FCSTD DOCUMENT  (FreeCAD 1.0R39109 (Git))
Label: assembly_01
License: All rights reserved
LicenseURL: https://en.wikipedia.org/wiki/All_rights_reserved
objects: App::FeaturePython×7, App::Link×3, Assembly::JointGroup×1, Assembly::AssemblyObject×1
EXTERNAL_REF file=case_bottom_01.FCStd obj=Body
EXTERNAL_REF file=case_top_01.FCStd obj=Body
EXTERNAL_REF file=device.FCStd obj=Body

FEATURE [App::Link] Body
  LinkedObject = -> <external case_bottom_01.FCStd>#Body
FEATURE [App::FeaturePython] GroundedJoint  # Assembly grounded joint (typed FeaturePython)
  ObjectToGround = -> Body
FEATURE [App::Link] Body001
  LinkPlacement = pos=(-0.499998,0.5,82.9001) rot=(0,0,1;0rad)
  LinkedObject = -> <external case_top_01.FCStd>#Body
  Placement = pos=(-0.499998,0.5,82.9001) rot=(0,0,1;0rad)
FEATURE [App::Link] Body002
  LinkPlacement = pos=(30.0639,41.1692,54.1501) rot=(0,0,0.985027;0.00293rad)
  LinkedObject = -> <external device.FCStd>#Body
  Placement = pos=(30.0639,41.1692,54.1501) rot=(0,0,0.985027;0.00293rad)
FEATURE [App::FeaturePython] Joint  label="Cylindrical"  # Assembly joint (typed FeaturePython)
  Activated = true
  AngleMax = 0
  AngleMin = 0
  Detach1 = false
  Detach2 = false
  Distance = 0
  Distance2 = 0
  EnableAngleMax = false
  EnableAngleMin = false
  EnableLengthMax = false
  EnableLengthMin = false
  JointType = 2 (Cylindrical)
  LengthMax = 0
  LengthMin = 0
  Placement1 = pos=(-24,-21.1,-12.65) rot=(1,0,0;3.14159rad)
  Placement2 = pos=(6.125,20,6.2) rot=(0,0,1;0rad)
  Reference1 = -> Assembly [Body002.Edge17,Body002.Edge17]
  Reference2 = -> Assembly [Body.?Face125,Body.?Face125]
FEATURE [App::FeaturePython] Joint001  label="Cylindrical001"  # Assembly joint (typed FeaturePython)
  Activated = true
  AngleMax = 0
  AngleMin = 0
  Detach1 = false
  Detach2 = false
  Distance = 0
  Distance2 = 0
  EnableAngleMax = false
  EnableAngleMin = false
  EnableLengthMax = false
  EnableLengthMin = false
  JointType = 2 (Cylindrical)
  LengthMax = 0
  LengthMin = 0
  Placement1 = pos=(-8.85,30.67,-11.775) rot=(1,0,0;3.14159rad)
  Placement2 = pos=(21.125,72,6.2) rot=(0,0,1;0rad)
  Reference1 = -> Assembly [Body002.Face63,Body002.Face63]
  Reference2 = -> Assembly [Body.?Face130,Body.?Face130]
FEATURE [App::FeaturePython] Joint002  label="Distance"  # Assembly joint (typed FeaturePython)
  Activated = true
  AngleMax = 0
  AngleMin = 0
  Detach1 = false
  Detach2 = false
  Distance = 2
  Distance2 = 0
  EnableAngleMax = false
  EnableAngleMin = false
  EnableLengthMax = false
  EnableLengthMin = false
  JointType = 5 (Distance)
  LengthMax = 0
  LengthMin = 0
  Placement1 = pos=(21.125,72,4.5) rot=(0,0,1;0rad)
  Placement2 = pos=(-0.0391973,-1.25732,-12.65) rot=(0,0,1;0rad)
  Reference1 = -> Assembly [Body.Face138,Body.Vertex194]
  Reference2 = -> Assembly [Body002.Face3,Body002.Edge42]
FEATURE [App::FeaturePython] Joint003  label="Distance001"  # Assembly joint (typed FeaturePython)
  Activated = true
  AngleMax = 0
  AngleMin = 0
  Detach1 = false
  Detach2 = false
  Distance = 0
  Distance2 = 0
  EnableAngleMax = false
  EnableAngleMin = false
  EnableLengthMax = false
  EnableLengthMin = false
  JointType = 5 (Distance)
  LengthMax = 0
  LengthMin = 0
  Placement1 = pos=(30,78,-0.75) rot=(1,0,0;1.5708rad)
  Placement2 = pos=(30,78.5,20.95) rot=(0,0.707107,0.707107;3.14159rad)
  Reference1 = -> Assembly [Body001.Face23,Body001.Vertex22]
  Reference2 = -> Assembly [Body.Face101,Body.Face101]
FEATURE [App::FeaturePython] Joint004  label="Distance002"  # Assembly joint (typed FeaturePython)
  Activated = true
  AngleMax = 0
  AngleMin = 0
  Detach1 = false
  Detach2 = false
  Distance = 0
  Distance2 = 0
  EnableAngleMax = false
  EnableAngleMin = false
  EnableLengthMax = false
  EnableLengthMin = false
  JointType = 5 (Distance)
  LengthMax = 0
  LengthMin = 0
  Placement1 = pos=(2,40,-0.75) rot=(0.57735,0.57735,0.57735;2.0944rad)
  Placement2 = pos=(1.5,40,20.95) rot=(-0.57735,0.57735,0.57735;4.18879rad)
  Reference1 = -> Assembly [Body001.Face21,Body001.Face21]
  Reference2 = -> Assembly [Body.Face98,Body.Face98]
FEATURE [App::FeaturePython] Joint005  label="Distance003"  # Assembly joint (typed FeaturePython)
  Activated = true
  AngleMax = 0
  AngleMin = 0
  Detach1 = false
  Detach2 = false
  Distance = 0
  Distance2 = 0
  EnableAngleMax = false
  EnableAngleMin = false
  EnableLengthMax = false
  EnableLengthMin = false
  JointType = 5 (Distance)
  LengthMax = 0
  LengthMin = 0
  Placement1 = pos=(30,40,-2) rot=(0,0,1;0rad)
  Placement2 = pos=(30,40,19.9) rot=(0,0,1;0rad)
  Reference1 = -> Assembly [Body001.Face5,Body001.Vertex18]
  Reference2 = -> Assembly [Body.Face64,Body.Vertex106]
FEATURE [Assembly::JointGroup] Joints
  Group = -> [GroundedJoint,Joint,Joint001,Joint002,Joint003,Joint004,Joint005]
FEATURE [Assembly::AssemblyObject] Assembly
  Group = -> [Joints,Body,GroundedJoint,Body001,Body002,Joint,Joint001,Joint002,Joint003,Joint004,Joint005]
  Origin = -> Origin
  Type = Assembly

RESOLVED EXTERNAL PARTS (link-assembly join: the EXTERNAL_REF files above that resolve inside this repo's crawl, each included once):
---- part case_bottom_01.FCStd = doc fcstd_fc7d65538bb1 ----
FCSTD DOCUMENT  (FreeCAD 1.0R39109 (Git))
Label: case_bottom_01
License: All rights reserved
LicenseURL: https://en.wikipedia.org/wiki/All_rights_reserved
objects: Sketcher::SketchObject×11, PartDesign::Fillet×8, PartDesign::Pad×5, PartDesign::Pocket×4, PartDesign::PolarPattern×1, PartDesign::LinearPattern×1, PartDesign::Body×1
note: 78 computed .brp shape members not serialized (recipe doc carries the construction recipe); baked Part::Feature solids carry a one-line shape summary decoded from their .brp

FEATURE [Sketcher::SketchObject] Sketch
  ArcFitTolerance = 1e-06
  AttachmentSupport = -> [XY_Plane]
  FullyConstrained = true
  MakeInternals = false
  MapMode = 5
  sketch-geometry (4):
    g0: LineSegment StartX=0 StartY=0 StartZ=0 EndX=60 EndY=0 EndZ=0
    g1: LineSegment StartX=60 StartY=0 StartZ=0 EndX=60 EndY=80 EndZ=0
    g2: LineSegment StartX=60 StartY=80 StartZ=0 EndX=0 EndY=80 EndZ=0
    g3: LineSegment StartX=0 StartY=80 StartZ=0 EndX=0 EndY=0 EndZ=0
  constraints (11):
    c: Coincident(g0,g1)
    c: Coincident(g1,g2)
    c: Coincident(g2,g3)
    c: Coincident(g3,g0)
    c: Horizontal(g0)
    c: Horizontal(g2)
    c: Vertical(g1)
    c: Vertical(g3)
    c: Coincident(g0,g-1)
    c: DistanceY(g1,g1) = 80
    c: DistanceX(g2,g2) = 60
FEATURE [PartDesign::Pad] Pad
  Direction = (0,0,1)
  Length = 2.5
  Length2 = 10
  Profile = -> Sketch
  ReferenceAxis = -> Sketch [N_Axis]
  Refine = true
  Suppressed = false
  Type = 0
FEATURE [Sketcher::SketchObject] Sketch001
  ArcFitTolerance = 1e-06
  AttachmentSupport = -> [Pad]
  ExternalGeometry = -> [Pad]
  FullyConstrained = true
  MakeInternals = false
  MapMode = 5
  Placement = pos=(0,0,2.5) rot=(0,0,1;0rad)
  sketch-geometry (8):
    g0: LineSegment StartX=0 StartY=80 StartZ=0 EndX=0 EndY=0 EndZ=0
    g1: LineSegment StartX=0 StartY=0 StartZ=0 EndX=60 EndY=0 EndZ=0
    g2: LineSegment StartX=60 StartY=0 StartZ=0 EndX=60 EndY=80 EndZ=0
    g3: LineSegment StartX=60 StartY=80 StartZ=0 EndX=0 EndY=80 EndZ=0
    g4: LineSegment StartX=2.5 StartY=77.5 StartZ=0 EndX=2.5 EndY=2.5 EndZ=0
    g5: LineSegment StartX=2.5 StartY=2.5 StartZ=0 EndX=57.5 EndY=2.5 EndZ=0
    g6: LineSegment StartX=57.5 StartY=2.5 StartZ=0 EndX=57.5 EndY=77.5 EndZ=0
    g7: LineSegment StartX=57.5 StartY=77.5 StartZ=0 EndX=2.5 EndY=77.5 EndZ=0
  constraints (22):
    c: Coincident(g0,g1)
    c: Coincident(g1,g2)
    c: Coincident(g2,g3)
    c: Coincident(g3,g0)
    c: Vertical(g0)
    c: Vertical(g2)
    c: Horizontal(g1)
    c: Horizontal(g3)
    c: Coincident(g0,g-5)
    c: Coincident(g1,g-6)
    c: Coincident(g4,g5)
    c: Coincident(g5,g6)
    c: Coincident(g6,g7)
    c: Coincident(g7,g4)
    c: Vertical(g4)
    c: Vertical(g6)
    c: Horizontal(g5)
    c: Horizontal(g7)
    c: Distance(g3,g7) = 2.5
    c: Distance(g0,g4) = 2.5
    c: Distance(g2,g6) = 2.5
    c: Distance(g1,g5) = 2.5
FEATURE [PartDesign::Pad] Pad001
  BaseFeature = -> Pad
  Direction = (0,0,1)
  Length = 19.5
  Length2 = 10
  Profile = -> Sketch001
  ReferenceAxis = -> Sketch001 [N_Axis]
  Refine = true
  Suppressed = false
  Type = 0
FEATURE [Sketcher::SketchObject] Sketch002
  ArcFitTolerance = 1e-06
  AttachmentSupport = -> [Pad001]
  FullyConstrained = true
  MakeInternals = false
  MapMode = 5
  Placement = pos=(0,0,2.5) rot=(0,0,1;0rad)
FEATURE [Sketcher::SketchObject] Sketch003
  ArcFitTolerance = 1e-06
  AttachmentSupport = -> [Pad001]
  ExternalGeometry = -> [Pad001]
  FullyConstrained = true
  MakeInternals = false
  MapMode = 5
  Placement = pos=(0,0,2.5) rot=(0,0,1;0rad)
  sketch-geometry (6):
    g0: Circle CenterX=21.125 CenterY=72 CenterZ=0 NormalX=0 NormalY=0 NormalZ=1 AngleXU=0 Radius=5
    g1: Circle CenterX=48.625 CenterY=72 CenterZ=0 NormalX=0 NormalY=0 NormalZ=1 AngleXU=0 Radius=5
    g2: Circle CenterX=6.125 CenterY=20 CenterZ=0 NormalX=0 NormalY=0 NormalZ=1 AngleXU=0 Radius=5
    g3: Circle CenterX=53.875 CenterY=21 CenterZ=0 NormalX=0 NormalY=0 NormalZ=1 AngleXU=0 Radius=5
    g4: LineSegment [constr] StartX=6.125 StartY=20 StartZ=0 EndX=2.5 EndY=20 EndZ=0
    g5: LineSegment [constr] StartX=53.875 StartY=21 StartZ=0 EndX=57.5 EndY=21 EndZ=0
  constraints (18):
    c: Equal(g0,g1)
    c: Equal(g0,g2)
    c: Equal(g0,g3)
    c: Diameter(g0) = 10
    c: Distance(g3,g-1) = 21
    c: Distance(g2,g-1) = 20
    c: DistanceY(g2,g0) = 52
    c: DistanceY(g2,g1) = 52
    c: Distance(g0,g1) = 27.5
    c: Coincident(g4,g2)
    c: PointOnObject(g4,g-5)
    c: Horizontal(g4)
    c: Coincident(g5,g3)
    c: PointOnObject(g5,g-4)
    c: Horizontal(g5)
    c: Equal(g5,g4)
    c: DistanceX(g2,g3) = 47.75
    c: DistanceX(g2,g0) = 15
FEATURE [PartDesign::Pad] Pad002
  BaseFeature = -> Pad001
  Direction = (0,0,1)
  Length = 2
  Length2 = 10
  Profile = -> Sketch003
  ReferenceAxis = -> Sketch003 [N_Axis]
  Refine = true
  Suppressed = false
  Type = 0
FEATURE [Sketcher::SketchObject] Sketch004
  ArcFitTolerance = 1e-06
  AttachmentSupport = -> [Pad002]
  ExternalGeometry = -> [Pad002]
  FullyConstrained = true
  MakeInternals = false
  MapMode = 5
  Placement = pos=(0,0,4.5) rot=(0,0,1;0rad)
  sketch-geometry (4):
    g0: Circle CenterX=21.125 CenterY=72 CenterZ=0 NormalX=0 NormalY=0 NormalZ=1 AngleXU=0 Radius=1.25
    g1: Circle CenterX=6.125 CenterY=20 CenterZ=0 NormalX=0 NormalY=0 NormalZ=1 AngleXU=0 Radius=1.25
    g2: Circle CenterX=53.875 CenterY=21 CenterZ=0 NormalX=0 NormalY=0 NormalZ=1 AngleXU=0 Radius=1.25
    g3: Circle CenterX=48.625 CenterY=72 CenterZ=0 NormalX=0 NormalY=0 NormalZ=1 AngleXU=0 Radius=1.25
  constraints (8):
    c: Coincident(g0,g-4)
    c: Coincident(g1,g-5)
    c: Coincident(g3,g-3)
    c: Equal(g0,g3)
    c: Equal(g1,g2)
    c: Equal(g2,g3)
    c: Diameter(g0) = 2.5
    c: Coincident(g2,g-6)
FEATURE [PartDesign::Pad] Pad003
  BaseFeature = -> Pad002
  Direction = (0,0,1)
  Length = 4
  Length2 = 10
  Profile = -> Sketch004
  ReferenceAxis = -> Sketch004 [N_Axis]
  Refine = true
  Suppressed = false
  Type = 0
FEATURE [Sketcher::SketchObject] Sketch005
  ArcFitTolerance = 1e-06
  AttachmentSupport = -> [Pad003]
  FullyConstrained = true
  MakeInternals = false
  MapMode = 5
  Placement = pos=(0,2.5,0) rot=(0,0.707107,0.707107;3.14159rad)
FEATURE [Sketcher::SketchObject] Sketch006
  ArcFitTolerance = 1e-06
  AttachmentSupport = -> [Pad003]
  ExternalGeometry = -> [Pad003]
  FullyConstrained = true
  MakeInternals = false
  MapMode = 5
  Placement = pos=(0,2.5,0) rot=(0,0.707107,0.707107;3.14159rad)
  sketch-geometry (4):
    g0: LineSegment StartX=-24.875 StartY=7.4 StartZ=0 EndX=-12.375 EndY=7.4 EndZ=0
    g1: LineSegment StartX=-12.375 StartY=7.4 StartZ=0 EndX=-12.375 EndY=18.9 EndZ=0
    g2: LineSegment StartX=-12.375 StartY=18.9 StartZ=0 EndX=-24.875 EndY=18.9 EndZ=0
    g3: LineSegment StartX=-24.875 StartY=18.9 StartZ=0 EndX=-24.875 EndY=7.4 EndZ=0
  constraints (12):
    c: Coincident(g0,g1)
    c: Coincident(g1,g2)
    c: Coincident(g2,g3)
    c: Coincident(g3,g0)
    c: Horizontal(g0)
    c: Horizontal(g2)
    c: Vertical(g1)
    c: Vertical(g3)
    c: Distance(g-4,g0) = 2.9
    c: Distance(g1,g3) = 12.5
    c: Distance(g2,g0) = 11.5
    c: Distance(g-6,g1) = 5
FEATURE [PartDesign::Pocket] Pocket
  BaseFeature = -> Pad003
  Direction = (0,-1,2e-16)
  Length = 5
  Length2 = 5
  Profile = -> Sketch006
  ReferenceAxis = -> Sketch006 [N_Axis]
  Refine = true
  Suppressed = false
  Type = 0
FEATURE [Sketcher::SketchObject] Sketch007
  ArcFitTolerance = 1e-06
  AttachmentSupport = -> [Pocket]
  ExternalGeometry = -> [Pocket]
  FullyConstrained = true
  MakeInternals = false
  MapMode = 5
  Placement = pos=(0,0,0) rot=(1,0,0;1.5708rad)
  sketch-geometry (5):
    g0: LineSegment StartX=43.875 StartY=7.4 StartZ=0 EndX=53.375 EndY=7.4 EndZ=0
    g1: LineSegment StartX=53.375 StartY=7.4 StartZ=0 EndX=53.375 EndY=18.6 EndZ=0
    g2: LineSegment StartX=53.375 StartY=18.6 StartZ=0 EndX=43.875 EndY=18.6 EndZ=0
    g3: LineSegment StartX=43.875 StartY=18.6 StartZ=0 EndX=43.875 EndY=7.4 EndZ=0
    g4: LineSegment [constr] StartX=24.875 StartY=7.4 StartZ=0 EndX=43.875 EndY=7.4 EndZ=0
  constraints (14):
    c: Coincident(g0,g1)
    c: Coincident(g1,g2)
    c: Coincident(g2,g3)
    c: Coincident(g3,g0)
    c: Horizontal(g0)
    c: Horizontal(g2)
    c: Vertical(g1)
    c: Vertical(g3)
    c: Distance(g-5,g3) = 19
    c: Distance(g2,g2) = 9.5
    c: Coincident(g4,g-4)
    c: Coincident(g4,g0)
    c: Horizontal(g4)
    c: Distance(g3,g3) = 11.2
FEATURE [PartDesign::Pocket] Pocket001
  BaseFeature = -> Pocket
  Direction = (0,1,-2e-16)
  Length = 5
  Length2 = 5
  Profile = -> Sketch007
  ReferenceAxis = -> Sketch007 [N_Axis]
  Refine = true
  Suppressed = false
  Type = 0
FEATURE [PartDesign::Fillet] Fillet
  Base = -> Pocket001 [Edge6,Edge5,Edge16,Edge18]
  BaseFeature = -> Pocket001
  Radius = 2
  Refine = true
  SupportTransform = false
  Suppressed = false
  UseAllEdges = false
FEATURE [PartDesign::Fillet] Fillet001
  Base = -> Fillet [Edge5,Edge1,Edge3,Edge4,Edge8,Edge2,Edge6,Edge7]
  BaseFeature = -> Fillet
  Radius = 2
  Refine = true
  SupportTransform = false
  Suppressed = false
  UseAllEdges = false
FEATURE [PartDesign::Fillet] Fillet002
  Base = -> Fillet001 [Edge100,Edge106,Edge108,Edge102]
  BaseFeature = -> Fillet001
  Radius = 0.6
  Refine = true
  SupportTransform = false
  Suppressed = false
  UseAllEdges = false
FEATURE [PartDesign::Fillet] Fillet003
  Base = -> Fillet002 [Edge6,Edge8,Edge49,Edge51,Edge53]
  BaseFeature = -> Fillet002
  Radius = 1
  Refine = true
  SupportTransform = false
  Suppressed = false
  UseAllEdges = false
FEATURE [PartDesign::Fillet] Fillet004
  Base = -> Fillet003 [Edge73,Edge75,Edge74,Edge72,Edge79,Edge78,Edge77,Edge76]
  BaseFeature = -> Fillet003
  Radius = 1
  Refine = true
  SupportTransform = false
  Suppressed = false
  UseAllEdges = false
FEATURE [Sketcher::SketchObject] Sketch008
  ArcFitTolerance = 1e-06
  AttachmentSupport = -> [Fillet004]
  ExternalGeometry = -> [Fillet004]
  FullyConstrained = true
  MakeInternals = false
  MapMode = 5
  Placement = pos=(0,0,22) rot=(0,0,1;0rad)
  sketch-geometry (8):
    g0: LineSegment StartX=1.5 StartY=78.5 StartZ=0 EndX=1.5 EndY=1.5 EndZ=0
    g1: LineSegment StartX=1.5 StartY=1.5 StartZ=0 EndX=58.5 EndY=1.5 EndZ=0
    g2: LineSegment StartX=58.5 StartY=1.5 StartZ=0 EndX=58.5 EndY=78.5 EndZ=0
    g3: LineSegment StartX=58.5 StartY=78.5 StartZ=0 EndX=1.5 EndY=78.5 EndZ=0
    g4: LineSegment StartX=0 StartY=80 StartZ=0 EndX=0 EndY=0 EndZ=0
    g5: LineSegment StartX=0 StartY=0 StartZ=0 EndX=60 EndY=0 EndZ=0
    g6: LineSegment StartX=60 StartY=0 StartZ=0 EndX=60 EndY=80 EndZ=0
    g7: LineSegment StartX=60 StartY=80 StartZ=0 EndX=0 EndY=80 EndZ=0
  constraints (24):
    c: Coincident(g0,g1)
    c: Coincident(g1,g2)
    c: Coincident(g2,g3)
    c: Coincident(g3,g0)
    c: Vertical(g0)
    c: Vertical(g2)
    c: Horizontal(g1)
    c: Horizontal(g3)
    c: Distance(g-6,g3) = 1.5
    c: Distance(g-3,g0) = 1.5
    c: Distance(g-4,g1) = 1.5
    c: Distance(g-5,g2) = 1.5
    c: Coincident(g4,g5)
    c: Coincident(g5,g6)
    c: Coincident(g6,g7)
    c: Coincident(g7,g4)
    c: Vertical(g4)
    c: Vertical(g6)
    c: Horizontal(g5)
    c: Horizontal(g7)
    c: PointOnObject(g6,g-5)
    c: PointOnObject(g4,g-3)
    c: PointOnObject(g4,g-4)
    c: PointOnObject(g6,g-6)
FEATURE [PartDesign::Pocket] Pocket002
  BaseFeature = -> Fillet004
  Direction = (0,0,-1)
  Length = 2.1
  Length2 = 5
  Profile = -> Sketch008
  ReferenceAxis = -> Sketch008 [N_Axis]
  Refine = true
  Suppressed = false
  Type = 0
FEATURE [PartDesign::Fillet] Fillet005
  Base = -> Pocket002 [Edge67,Edge69,Edge65,Edge105,Edge64,Edge91,Edge88,Edge122]
  BaseFeature = -> Pocket002
  Radius = 1
  Refine = true
  SupportTransform = false
  Suppressed = false
  UseAllEdges = false
FEATURE [PartDesign::PolarPattern] PolarPattern
  Angle = 360
  Axis = -> Z_Axis
  BaseFeature = -> Fillet005
  Mode = 0
  Occurrences = 2
  Offset = 120
  Refine = true
  Suppressed = false
  TransformMode = 1
FEATURE [Sketcher::SketchObject] Sketch009
  ArcFitTolerance = 1e-06
  AttachmentSupport = -> [PolarPattern]
  ExternalGeometry = -> [PolarPattern]
  FullyConstrained = true
  MakeInternals = false
  MapMode = 5
  Placement = pos=(0,0,2.5) rot=(0,0,1;0rad)
  sketch-geometry (4):
    g0: ArcOfCircle CenterX=12.5 CenterY=56.25 CenterZ=0 NormalX=0 NormalY=0 NormalZ=1 AngleXU=0 Radius=1.25 StartAngle=1.5708 EndAngle=4.71239
    g1: ArcOfCircle CenterX=47.5 CenterY=56.25 CenterZ=0 NormalX=0 NormalY=0 NormalZ=1 AngleXU=0 Radius=1.25 StartAngle=4.71239 EndAngle=7.85398
    g2: LineSegment StartX=12.5 StartY=57.5 StartZ=0 EndX=47.5 EndY=57.5 EndZ=0
    g3: LineSegment StartX=12.5 StartY=55 StartZ=0 EndX=47.5 EndY=55 EndZ=0
  constraints (10):
    c: Tangent(g0,g2) = 1.5708
    c: Tangent(g0,g3) = -1.5708
    c: Tangent(g1,g2) = 1.5708
    c: Tangent(g1,g3) = -1.5708
    c: Equal(g0,g1)
    c: Horizontal(g2)
    c: Distance(g0,g-4) = 10
    c: Distance(g1,g-3) = 10
    c: Distance(g2,g3) = 2.5
    c: Distance(g-5,g2) = 20
FEATURE [PartDesign::Pocket] Pocket003
  BaseFeature = -> PolarPattern
  Direction = (0,0,-1)
  Length = 5
  Length2 = 5
  Profile = -> Sketch009
  ReferenceAxis = -> Sketch009 [N_Axis]
  Refine = true
  Suppressed = false
  Type = 0
FEATURE [PartDesign::LinearPattern] LinearPattern
  BaseFeature = -> Pocket003
  Direction = -> Y_Axis
  Length = 28
  Mode = 1
  Occurrences = 5
  Offset = 7
  Originals = -> [Pocket003]
  Refine = true
  Reversed = true
  Suppressed = false
  TransformMode = 0
FEATURE [PartDesign::Fillet] Fillet006
  Base = -> LinearPattern [Edge137,Edge139,Edge138,Edge136,Edge141,Edge142,Edge143,Edge140,Edge147,Edge146,Edge144,Edge151,Edge150,Edge149,Edge148,Edge145,Edge154,Edge153,Edge155,Edge152,Edge166,Edge168,Edge165,Edge167,Edge171,Edge172,Edge170,Edge169,Edge174,Edge173,Edge176,Edge175,Edge178,Edge180,Edge179,Edge177,Edge183,Edge181,Edge182,Edge184]
  BaseFeature = -> LinearPattern
  Radius = 1
  Refine = true
  SupportTransform = false
  Suppressed = false
  UseAllEdges = false
FEATURE [Sketcher::SketchObject] Sketch010
  ArcFitTolerance = 1e-06
  AttachmentSupport = -> [Fillet006]
  ExternalGeometry = -> [Fillet006]
  FullyConstrained = false
  MakeInternals = false
  MapMode = 5
  Placement = pos=(0,0,0) rot=(1,0,0;3.14159rad)
  sketch-geometry (8):
    g0: Circle CenterX=9.5 CenterY=-9.5 CenterZ=0 NormalX=0 NormalY=0 NormalZ=1 AngleXU=0 Radius=4.87662
    g1: Circle CenterX=50.5 CenterY=-9.5 CenterZ=0 NormalX=0 NormalY=0 NormalZ=1 AngleXU=0 Radius=4.87662
    g2: Circle CenterX=50.5 CenterY=-70.5 CenterZ=0 NormalX=0 NormalY=0 NormalZ=1 AngleXU=0 Radius=4.87662
    g3: Circle CenterX=9.5 CenterY=-70.5 CenterZ=0 NormalX=0 NormalY=0 NormalZ=1 AngleXU=0 Radius=4.87662
    g4: LineSegment [constr] StartX=50.5 StartY=-9.5 StartZ=0 EndX=50.5 EndY=-70.5 EndZ=0
    g5: LineSegment [constr] StartX=50.5 StartY=-70.5 StartZ=0 EndX=9.5 EndY=-70.5 EndZ=0
    g6: LineSegment [constr] StartX=9.5 StartY=-70.5 StartZ=0 EndX=9.5 EndY=-9.5 EndZ=0
    g7: LineSegment [constr] StartX=9.5 StartY=-9.5 StartZ=0 EndX=50.5 EndY=-9.5 EndZ=0
  constraints (19):
    c: Equal(g0,g1)
    c: Equal(g0,g3)
    c: Equal(g1,g2)
    c: Distance(g0,g-3) = 7.5
    c: Distance(g0,g-6) = 7.5
    c: Distance(g1,g-3) = 7.5
    c: Distance(g1,g-4) = 7.5
    c: Coincident(g4,g1)
    c: Coincident(g4,g2)
    c: Vertical(g4)
    c: Coincident(g5,g2)
    c: Coincident(g5,g3)
    c: Horizontal(g5)
    c: Coincident(g6,g3)
    c: Coincident(g6,g0)
    c: Vertical(g6)
    c: Coincident(g7,g0)
    c: Coincident(g7,g1)
    c: Distance(g2,g-5) = 7.5
FEATURE [PartDesign::Pad] Pad004
  BaseFeature = -> Fillet006
  Direction = (0,0,-1)
  Length = 2
  Length2 = 10
  Profile = -> Sketch010
  ReferenceAxis = -> Sketch010 [N_Axis]
  Refine = true
  Suppressed = false
  Type = 0
FEATURE [PartDesign::Fillet] Fillet007
  Base = -> Pad004 [Edge42,Edge60,Edge88,Edge86]
  BaseFeature = -> Pad004
  Radius = 1
  Refine = true
  SupportTransform = false
  Suppressed = false
  UseAllEdges = false
FEATURE [PartDesign::Body] Body
  AllowCompound = false
  Group = -> [Sketch,Pad,Sketch001,Pad001,Sketch003,Pad002,Sketch004,Pad003,Sketch005,Sketch006,Pocket,Sketch007,Pocket001,Fillet,Fillet001,Fillet002,Fillet003,Fillet004,Sketch008,Pocket002,Fillet005,PolarPattern,Sketch009,Pocket003,LinearPattern,Fillet006,Sketch010,Pad004,Fillet007]
  Origin = -> Origin
  Tip = -> Fillet007
---- part case_top_01.FCStd = doc fcstd_37e1c08d6b9f ----
FCSTD DOCUMENT  (FreeCAD 1.0R39109 (Git))
Label: case_top_01
License: All rights reserved
LicenseURL: https://en.wikipedia.org/wiki/All_rights_reserved
objects: PartDesign::Fillet×6, Sketcher::SketchObject×4, PartDesign::Pad×2, PartDesign::Pocket×2, PartDesign::Body×1
note: 39 computed .brp shape members not serialized (recipe doc carries the construction recipe); baked Part::Feature solids carry a one-line shape summary decoded from their .brp

FEATURE [Sketcher::SketchObject] Sketch003
  ArcFitTolerance = 1e-06
  AttachmentSupport = -> [XY_Plane]
  FullyConstrained = true
  MakeInternals = false
  MapMode = 5
  sketch-geometry (4):
    g0: LineSegment StartX=0 StartY=0 StartZ=0 EndX=60 EndY=0 EndZ=0
    g1: LineSegment StartX=60 StartY=0 StartZ=0 EndX=60 EndY=80 EndZ=0
    g2: LineSegment StartX=60 StartY=80 StartZ=0 EndX=0 EndY=80 EndZ=0
    g3: LineSegment StartX=0 StartY=80 StartZ=0 EndX=0 EndY=0 EndZ=0
  constraints (11):
    c: Coincident(g0,g1)
    c: Coincident(g1,g2)
    c: Coincident(g2,g3)
    c: Coincident(g3,g0)
    c: Horizontal(g0)
    c: Horizontal(g2)
    c: Vertical(g1)
    c: Vertical(g3)
    c: Coincident(g0,g-1)
    c: DistanceY(g1,g1) = 80
    c: DistanceX(g2,g2) = 60
FEATURE [PartDesign::Pad] Pad
  Direction = (0,0,1)
  Length = 2.5
  Length2 = 10
  Profile = -> Sketch003
  ReferenceAxis = -> Sketch003 [N_Axis]
  Refine = true
  Suppressed = false
  Type = 0
FEATURE [Sketcher::SketchObject] Sketch
  ArcFitTolerance = 1e-06
  AttachmentSupport = -> [Pad]
  ExternalGeometry = -> [Pad]
  FullyConstrained = true
  MakeInternals = false
  MapMode = 5
  Placement = pos=(0,0,2.5) rot=(0,0,1;0rad)
  sketch-geometry (6):
    g0: LineSegment StartX=8.5 StartY=71.3 StartZ=0 EndX=8.5 EndY=11 EndZ=0
    g1: LineSegment StartX=8.5 StartY=11 StartZ=0 EndX=51.5 EndY=11 EndZ=0
    g2: LineSegment StartX=51.5 StartY=11 StartZ=0 EndX=51.5 EndY=71.3 EndZ=0
    g3: LineSegment StartX=51.5 StartY=71.3 StartZ=0 EndX=8.5 EndY=71.3 EndZ=0
    g4: LineSegment [constr] StartX=8.5 StartY=11 StartZ=0 EndX=0 EndY=11 EndZ=0
    g5: LineSegment [constr] StartX=51.5 StartY=11 StartZ=0 EndX=60 EndY=11 EndZ=0
  constraints (18):
    c: Coincident(g0,g1)
    c: Coincident(g1,g2)
    c: Coincident(g2,g3)
    c: Coincident(g3,g0)
    c: Vertical(g0)
    c: Vertical(g2)
    c: Horizontal(g1)
    c: Horizontal(g3)
    c: Distance(g0,g2) = 43
    c: Distance(g1,g3) = 60.3
    c: Distance(g-5,g1) = 11
    c: Coincident(g4,g0)
    c: PointOnObject(g4,g-6)
    c: Coincident(g5,g1)
    c: PointOnObject(g5,g-4)
    c: Horizontal(g5)
    c: Horizontal(g4)
    c: Equal(g4,g5)
FEATURE [PartDesign::Pocket] Pocket
  BaseFeature = -> Pad
  Direction = (0,0,-1)
  Length = 5
  Length2 = 5
  Profile = -> Sketch
  ReferenceAxis = -> Sketch [N_Axis]
  Refine = true
  Suppressed = false
  Type = 0
FEATURE [Sketcher::SketchObject] Sketch004
  ArcFitTolerance = 1e-06
  AttachmentSupport = -> [Pocket]
  ExternalGeometry = -> [Pocket]
  FullyConstrained = true
  MakeInternals = false
  MapMode = 5
  Placement = pos=(0,0,0) rot=(1,0,0;3.14159rad)
  sketch-geometry (8):
    g0: LineSegment StartX=0 StartY=0 StartZ=0 EndX=0 EndY=-80 EndZ=0
    g1: LineSegment StartX=0 StartY=-80 StartZ=0 EndX=60 EndY=-80 EndZ=0
    g2: LineSegment StartX=60 StartY=-80 StartZ=0 EndX=60 EndY=0 EndZ=0
    g3: LineSegment StartX=60 StartY=0 StartZ=0 EndX=0 EndY=0 EndZ=0
    g4: LineSegment StartX=2 StartY=-2 StartZ=0 EndX=2 EndY=-78 EndZ=0
    g5: LineSegment StartX=2 StartY=-78 StartZ=0 EndX=58 EndY=-78 EndZ=0
    g6: LineSegment StartX=58 StartY=-78 StartZ=0 EndX=58 EndY=-2 EndZ=0
    g7: LineSegment StartX=58 StartY=-2 StartZ=0 EndX=2 EndY=-2 EndZ=0
  constraints (22):
    c: Coincident(g0,g1)
    c: Coincident(g1,g2)
    c: Coincident(g2,g3)
    c: Coincident(g3,g0)
    c: Vertical(g0)
    c: Vertical(g2)
    c: Horizontal(g1)
    c: Horizontal(g3)
    c: Coincident(g4,g5)
    c: Coincident(g5,g6)
    c: Coincident(g6,g7)
    c: Coincident(g7,g4)
    c: Vertical(g4)
    c: Vertical(g6)
    c: Horizontal(g5)
    c: Horizontal(g7)
    c: Distance(g3,g7) = 2
    c: Distance(g2,g6) = 2
    c: Distance(g1,g5) = 2
    c: Distance(g0,g4) = 2
    c: Coincident(g1,g-5)
    c: Coincident(g0,g-1)
FEATURE [PartDesign::Pad] Pad001
  BaseFeature = -> Pocket
  Direction = (0,0,-1)
  Length = 2
  Length2 = 10
  Profile = -> Sketch004
  ReferenceAxis = -> Sketch004 [N_Axis]
  Refine = true
  Suppressed = false
  Type = 0
FEATURE [Sketcher::SketchObject] Sketch005
  ArcFitTolerance = 1e-06
  AttachmentSupport = -> [Pad001]
  ExternalGeometry = -> [Pad001]
  FullyConstrained = true
  MakeInternals = false
  MapMode = 5
  Placement = pos=(0,0,2.5) rot=(0,0,1;0rad)
  sketch-geometry (4):
    g0: LineSegment StartX=24 StartY=4 StartZ=0 EndX=31.2 EndY=4 EndZ=0
    g1: LineSegment StartX=31.2 StartY=4 StartZ=0 EndX=31.2 EndY=8 EndZ=0
    g2: LineSegment StartX=31.2 StartY=8 StartZ=0 EndX=24 EndY=8 EndZ=0
    g3: LineSegment StartX=24 StartY=8 StartZ=0 EndX=24 EndY=4 EndZ=0
  constraints (12):
    c: Coincident(g0,g1)
    c: Coincident(g1,g2)
    c: Coincident(g2,g3)
    c: Coincident(g3,g0)
    c: Horizontal(g0)
    c: Horizontal(g2)
    c: Vertical(g1)
    c: Vertical(g3)
    c: Distance(g-3,g2) = 3
    c: Distance(g2,g0) = 4
    c: Distance(g-3,g3) = 15.5
    c: Distance(g0,g0) = 7.2
FEATURE [PartDesign::Pocket] Pocket001
  BaseFeature = -> Pad001
  Direction = (0,0,-1)
  Length = 5
  Length2 = 5
  Profile = -> Sketch005
  ReferenceAxis = -> Sketch005 [N_Axis]
  Refine = true
  Suppressed = false
  Type = 0
FEATURE [PartDesign::Fillet] Fillet
  Base = -> Pocket001 [Edge14,Edge10,Edge9,Edge12]
  BaseFeature = -> Pocket001
  Radius = 2
  Refine = true
  SupportTransform = false
  Suppressed = false
  UseAllEdges = false
FEATURE [PartDesign::Fillet] Fillet001
  Base = -> Fillet [Edge43,Edge41,Edge42,Edge44]
  BaseFeature = -> Fillet
  Radius = 1
  Refine = true
  SupportTransform = false
  Suppressed = false
  UseAllEdges = false
FEATURE [PartDesign::Fillet] Fillet002
  Base = -> Fillet001 [Edge13,Edge16,Edge15,Edge14]
  BaseFeature = -> Fillet001
  Radius = 1
  Refine = true
  SupportTransform = false
  Suppressed = false
  UseAllEdges = false
FEATURE [PartDesign::Fillet] Fillet003
  Base = -> Fillet002 [Edge9,Edge11,Edge13,Edge10,Edge12,Edge15,Edge16,Edge14]
  BaseFeature = -> Fillet002
  Radius = 2
  Refine = true
  SupportTransform = false
  Suppressed = false
  UseAllEdges = false
FEATURE [PartDesign::Fillet] Fillet004
  Base = -> Fillet003 [Edge84,Edge83,Edge82,Edge81]
  BaseFeature = -> Fillet003
  Radius = 0.5
  Refine = true
  SupportTransform = false
  Suppressed = false
  UseAllEdges = false
FEATURE [PartDesign::Fillet] Fillet005
  Base = -> Fillet004 [Edge39,Edge37,Edge43,Edge40]
  BaseFeature = -> Fillet004
  Radius = 1.1
  Refine = true
  SupportTransform = false
  Suppressed = false
  UseAllEdges = false
FEATURE [PartDesign::Body] Body
  AllowCompound = false
  Group = -> [Sketch003,Pad,Sketch,Pocket,Sketch004,Pad001,Sketch005,Pocket001,Fillet,Fillet001,Fillet002,Fillet003,Fillet004,Fillet005]
  Origin = -> Origin
  Tip = -> Fillet005
---- part device.FCStd = doc fcstd_5e4a5b32eaac (72770 chars; too large to inline — full recipe in that document) ----
